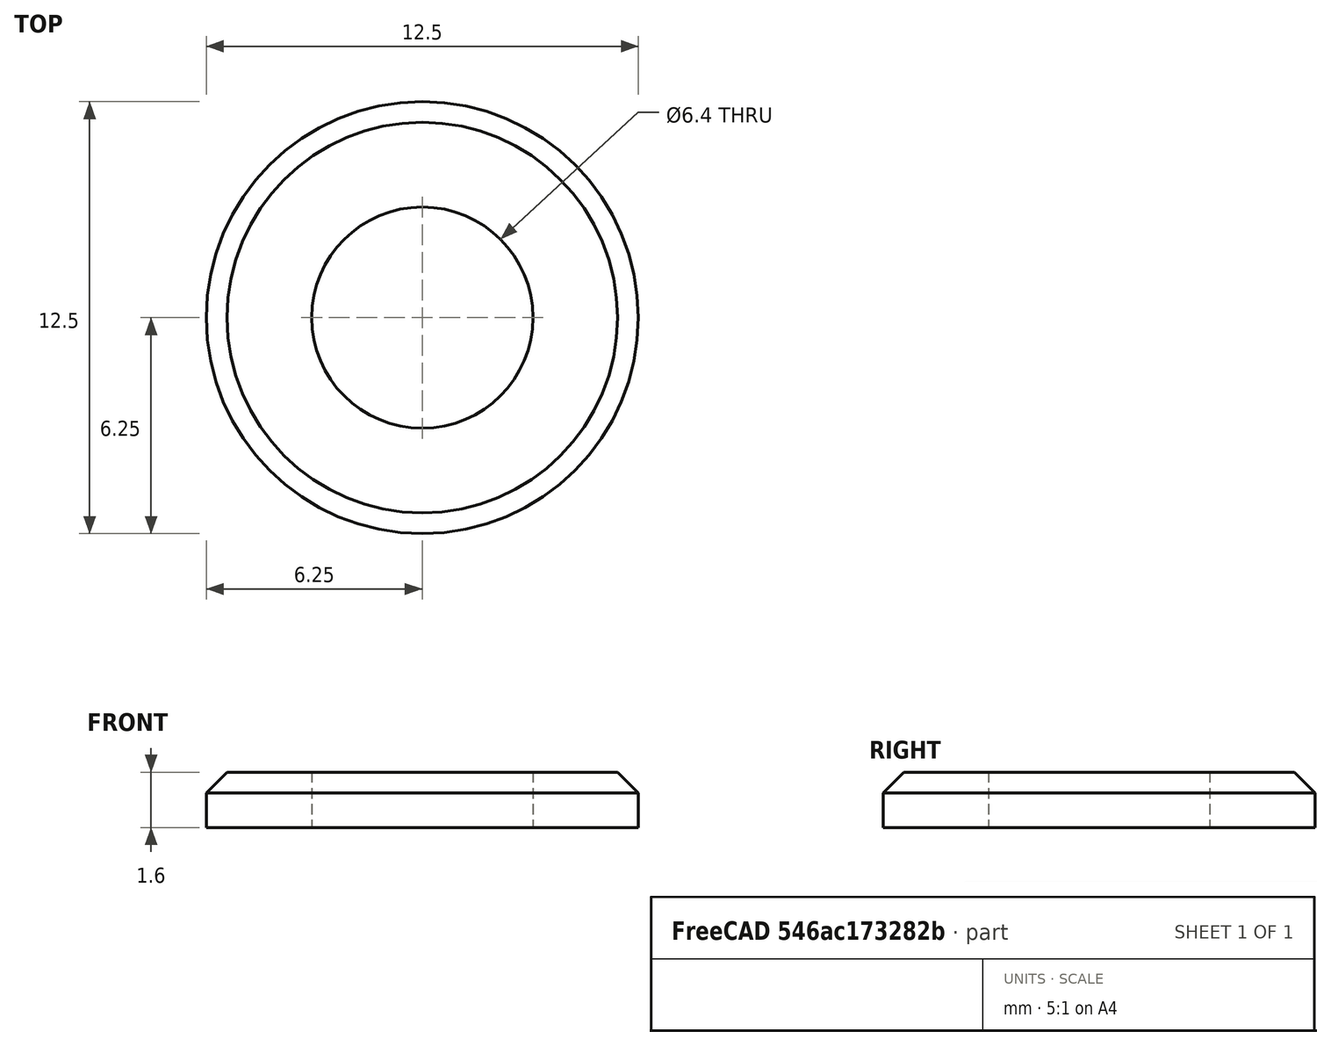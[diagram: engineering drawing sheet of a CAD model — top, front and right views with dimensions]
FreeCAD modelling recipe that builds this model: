
FCSTD DOCUMENT  (FreeCAD 0.15R4651 (Git))
Label: Scheibe_DIN125-B 6,4
License: CC-BY 3.0
LicenseURL: http://creativecommons.org/licenses/by/3.0/
objects: Sketcher::SketchObject×1, PartDesign::Revolution×1
note: 3 computed .brp shape members not serialized (recipe doc carries the construction recipe); baked Part::Feature solids carry a one-line shape summary decoded from their .brp

FEATURE [Sketcher::SketchObject] Sketch
  Placement = pos=(0,0,0) rot=(0.57735,0.57735,0.57735;2.0944rad)
  sketch-geometry (5):
    g0: LineSegment StartX=3.2 StartY=0 StartZ=0 EndX=6.25 EndY=0 EndZ=0
    g1: LineSegment StartX=6.25 StartY=0 StartZ=0 EndX=6.25 EndY=1 EndZ=0
    g2: LineSegment StartX=5.65 StartY=1.6 StartZ=0 EndX=3.2 EndY=1.6 EndZ=0
    g3: LineSegment StartX=3.2 StartY=1.6 StartZ=0 EndX=3.2 EndY=0 EndZ=0
    g4: LineSegment StartX=5.65 StartY=1.6 StartZ=0 EndX=6.25 EndY=1 EndZ=0
  constraints (15):
    c: Coincident(g0,g1)
    c: Coincident(g2,g3)
    c: Coincident(g3,g0)
    c: Horizontal(g0)
    c: Horizontal(g2)
    c: Vertical(g1)
    c: Vertical(g3)
    c: PointOnObject(g0,g-1)
    c: DistanceX(g-1,g2) = 3.2
    c: Coincident(g1,g4)
    c: Coincident(g2,g4)
    c: DistanceY(g3) = -1.6
    c: DistanceX(g-1,g1) = 6.25
    c: DistanceX(g4) = 0.6
    c: DistanceY(g4) = -0.6
FEATURE [PartDesign::Revolution] Revolution  label="Scheibe DIN 125 - B 6,4 #"
  Angle = 360
  Axis = (0,0,1)
  Base = (0,0,0)
  Placement = pos=(0,0,0) rot=(0.57735,0.57735,0.57735;2.0944rad)
  ReferenceAxis = -> Sketch [V_Axis]
  Reversed = true
  Sketch = -> Sketch
